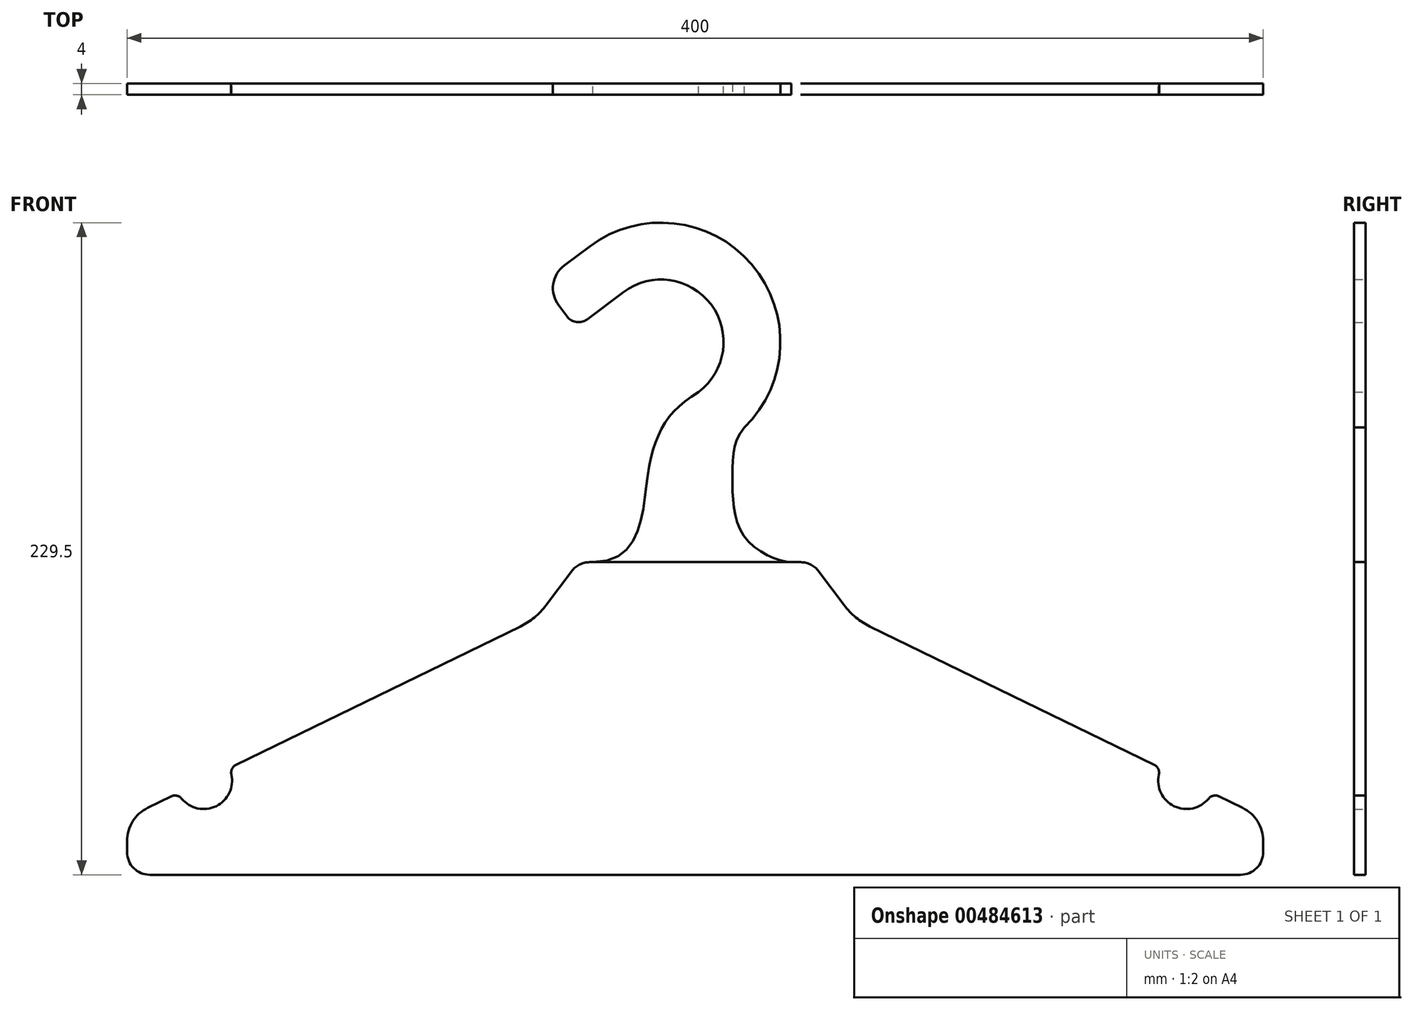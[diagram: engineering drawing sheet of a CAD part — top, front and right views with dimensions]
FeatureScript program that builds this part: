
annotation { "Feature Type Name" : "Feature", "Feature Type Description" : "" }
export const myFeature = defineFeature(function(context is Context, id is Id, definition is map)
    precondition{}
    {
        {
            var Q0;
            Q0=qCreatedBy(makeId("Front.planeOp"),FACE);
            var sketch = newSketch(context, id + "F0", { "sketchPlane" : qUnion([Q0])});
            skLineSegment(sketch, "E0", {"start": v(0, 0) * mm, "end": v(-192, 0) * mm});
            skLineSegment(sketch, "E1", {"start": v(-200, 8) * mm, "end": v(-200, 11.87) * mm});
            skLineSegment(sketch, "E2", {"start": v(-192.69, 23.56) * mm, "end": v(-184.4, 27.6) * mm});
            skLineSegment(sketch, "E3", {"start": v(-52.5, 94.84) * mm, "end": v(-43.53, 106.8) * mm});
            skLineSegment(sketch, "E4", {"start": v(-37.13, 110) * mm, "end": v(0, 110) * mm});
            skArc(sketch, "E5", {"start": v(-180.76, 26.8) * mm, "mid": v(-168.65, 24.13) * mm, "end": v(-163.26, 35.3) * mm});
            skPoint(sketch, "E6.visualSharp", {"position": v(-56.13, 90) * mm});
            skArc(sketch, "E6.filletArc", {"start": v(-61.56, 87.36) * mm, "mid": v(-56.58, 90.56) * mm, "end": v(-52.5, 94.84) * mm});
            skPoint(sketch, "E7.visualSharp", {"position": v(-41.13, 110) * mm});
            skArc(sketch, "E7.filletArc", {"start": v(-37.13, 110) * mm, "mid": v(-40.7, 109.16) * mm, "end": v(-43.53, 106.8) * mm});
            skPoint(sketch, "E8.visualSharp", {"position": v(-200, 20) * mm});
            skArc(sketch, "E8.filletArc", {"start": v(-192.69, 23.56) * mm, "mid": v(-198.02, 18.76) * mm, "end": v(-200, 11.87) * mm});
            skLineSegment(sketch, "E9.trimOffspring", {"start": v(-161.65, 38.66) * mm, "end": v(-61.56, 87.36) * mm});
            skPoint(sketch, "E10.visualSharp", {"position": v(-182.02, 28.75) * mm});
            skArc(sketch, "E10.filletArc", {"start": v(-180.76, 26.8) * mm, "mid": v(-182.44, 27.82) * mm, "end": v(-184.4, 27.6) * mm});
            skPoint(sketch, "E11.visualSharp", {"position": v(-164.03, 37.5) * mm});
            skArc(sketch, "E11.filletArc", {"start": v(-161.65, 38.66) * mm, "mid": v(-163.04, 37.26) * mm, "end": v(-163.26, 35.3) * mm});
            skPoint(sketch, "E12.visualSharp", {"position": v(-200, 0) * mm});
            skArc(sketch, "E12.filletArc", {"start": v(-200, 8) * mm, "mid": v(-197.66, 2.34) * mm, "end": v(-192, 0) * mm});
            skArc(sketch, "E13.MirrorCS", {"start": v(161.65, 38.66) * mm, "mid": v(163.04, 37.26) * mm, "end": v(163.26, 35.3) * mm});
            skArc(sketch, "E14.MirrorCS", {"start": v(180.76, 26.8) * mm, "mid": v(182.44, 27.82) * mm, "end": v(184.4, 27.6) * mm});
            skArc(sketch, "E15.MirrorCS", {"start": v(200, 8) * mm, "mid": v(197.66, 2.34) * mm, "end": v(192, 0) * mm});
            skArc(sketch, "E16.MirrorCS", {"start": v(37.13, 110) * mm, "mid": v(40.7, 109.16) * mm, "end": v(43.53, 106.8) * mm});
            skLineSegment(sketch, "E17.MirrorCS", {"start": v(192.69, 23.56) * mm, "end": v(184.4, 27.6) * mm});
            skLineSegment(sketch, "E18.MirrorCS", {"start": v(200, 8) * mm, "end": v(200, 11.87) * mm});
            skArc(sketch, "E19.MirrorCS", {"start": v(192.69, 23.56) * mm, "mid": v(198.02, 18.76) * mm, "end": v(200, 11.87) * mm});
            skArc(sketch, "E20.MirrorCS", {"start": v(61.56, 87.36) * mm, "mid": v(56.58, 90.56) * mm, "end": v(52.5, 94.84) * mm});
            skPoint(sketch, "E21.MirrorP", {"position": v(56.13, 90) * mm});
            skLineSegment(sketch, "E22.MirrorCS", {"start": v(161.65, 38.66) * mm, "end": v(61.56, 87.36) * mm});
            skArc(sketch, "E23.MirrorCS", {"start": v(180.76, 26.8) * mm, "mid": v(168.65, 24.13) * mm, "end": v(163.26, 35.3) * mm});
            skLineSegment(sketch, "E24.MirrorCS", {"start": v(37.13, 110) * mm, "end": v(0, 110) * mm});
            skLineSegment(sketch, "E25.MirrorCS", {"start": v(52.5, 94.84) * mm, "end": v(43.53, 106.8) * mm});
            skPoint(sketch, "E26.MirrorP", {"position": v(182.02, 28.75) * mm});
            skPoint(sketch, "E27.MirrorP", {"position": v(41.13, 110) * mm});
            skPoint(sketch, "E28.MirrorP", {"position": v(164.03, 37.5) * mm});
            skPoint(sketch, "E29.MirrorP", {"position": v(200, 0) * mm});
            skPoint(sketch, "E30.MirrorP", {"position": v(200, 20) * mm});
            skLineSegment(sketch, "E31.MirrorCS", {"start": v(0, 0) * mm, "end": v(192, 0) * mm});
            skSolve(sketch);
        }
        {
            var Q0;
            Q0=qCreatedBy(makeId("Front.planeOp"),FACE);
            var sketch = newSketch(context, id + "F1", { "sketchPlane" : qUnion([Q0])});
            skPoint(sketch, "E32.0", {"position": v(0, 110) * mm});
            skLineSegment(sketch, "E33", {"start": v(0, 110) * mm, "end": v(0, 151.5) * mm});
            skArc(sketch, "E34", {"start": v(6, 163.5) * mm, "mid": v(12, 205.5) * mm, "end": v(-30, 211.5) * mm});
            skLineSegment(sketch, "E35", {"start": v(-30, 211.5) * mm, "end": v(-41.2, 203.1) * mm});
            skPoint(sketch, "E36.visualSharp", {"position": v(0, 160) * mm});
            skArc(sketch, "E36.filletArc", {"start": v(6, 163.5) * mm, "mid": v(1.58, 158.2) * mm, "end": v(0, 151.5) * mm});
            skLineSegment(sketch, "E37.0", {"start": v(-37.2, 221.1) * mm, "end": v(-46.06, 214.45) * mm});
            skArc(sketch, "E37.1", {"start": v(13.2, 153.9) * mm, "mid": v(21.6, 212.7) * mm, "end": v(-37.2, 221.1) * mm});
            skArc(sketch, "E37.2", {"start": v(13.2, 153.9) * mm, "mid": v(12.32, 152.84) * mm, "end": v(12, 151.5) * mm});
            skLineSegment(sketch, "E37.3", {"start": v(12, 110) * mm, "end": v(12, 151.5) * mm});
            skLineSegment(sketch, "E38.0", {"start": v(-25.2, 205.1) * mm, "end": v(-38.06, 195.45) * mm});
            skArc(sketch, "E38.1", {"start": v(1.2, 169.9) * mm, "mid": v(5.6, 200.7) * mm, "end": v(-25.2, 205.1) * mm});
            skArc(sketch, "E38.2", {"start": v(1.2, 169.9) * mm, "mid": v(-5.57, 161.78) * mm, "end": v(-8, 151.5) * mm});
            skLineSegment(sketch, "E38.3", {"start": v(-8, 110) * mm, "end": v(-8, 151.5) * mm});
            skLineSegment(sketch, "E39", {"start": v(-45.06, 196.45) * mm, "end": v(-48.06, 200.45) * mm});
            skPoint(sketch, "E40.visualSharp", {"position": v(-42.06, 192.45) * mm});
            skArc(sketch, "E40.filletArc", {"start": v(-45.06, 196.45) * mm, "mid": v(-41.77, 194.5) * mm, "end": v(-38.06, 195.45) * mm});
            skPoint(sketch, "E41.visualSharp", {"position": v(-54.06, 208.45) * mm});
            skArc(sketch, "E41.filletArc", {"start": v(-46.06, 214.45) * mm, "mid": v(-49.96, 207.87) * mm, "end": v(-48.06, 200.45) * mm});
            skLineSegment(sketch, "E42.0", {"start": v(37.13, 110) * mm, "end": v(0, 110) * mm});
            skLineSegment(sketch, "E42.1", {"start": v(-37.13, 110) * mm, "end": v(0, 110) * mm});
            skFitSpline(sketch, "E43", {"points": [v(-36.06, 110) * mm, v(-17.2, 136.96) * mm, v(-11.34, 157.85) * mm, v(1.2, 169.9) * mm], "startDerivative": vector(126.71, 0) * mm, "endDerivative": vector(61.94, 38.12) * mm});
            skFitSpline(sketch, "E44", {"points": [v(18.83, 158.98) * mm, v(13.1, 140.12) * mm, v(17.87, 118.31) * mm, v(33.81, 110) * mm], "startDerivative": vector(-51.04, -46.04) * mm, "endDerivative": vector(38.23, 0) * mm});
            skSolve(sketch);
        }
        {
            var Q0;
            Q0 = qSketchRegion(id + "F1", true);
            var Q1;
            Q1 = qSketchRegion(id + "F0", true);
            extrude(context, id + "F2", {"entities" : qUnion([Q0, Q1]), "depth" : 4 * mm});
        }
    });
